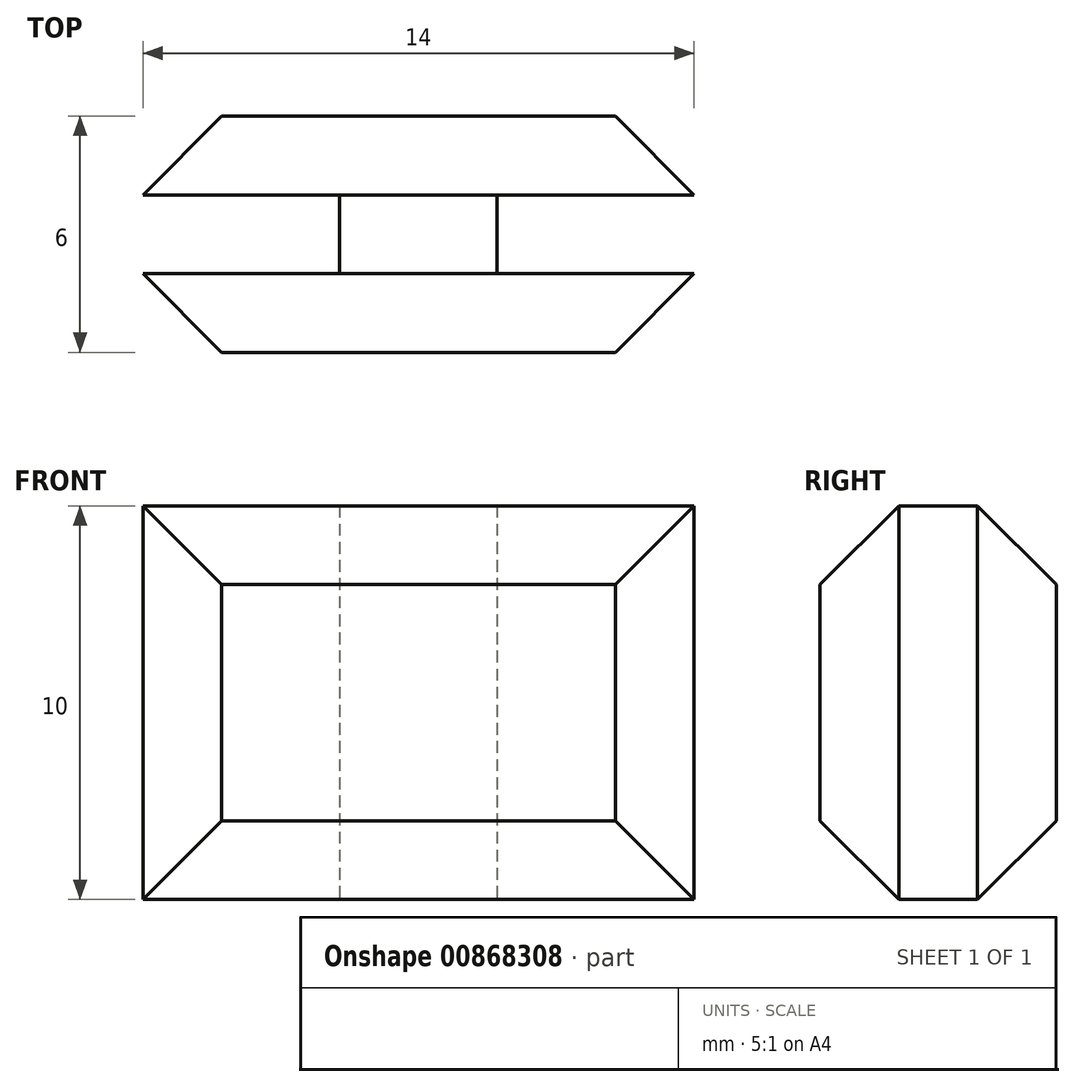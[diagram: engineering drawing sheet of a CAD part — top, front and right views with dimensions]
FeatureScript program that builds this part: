
annotation { "Feature Type Name" : "Feature", "Feature Type Description" : "" }
export const myFeature = defineFeature(function(context is Context, id is Id, definition is map)
    precondition{}
    {
        {
            var Q0;
            Q0=qCreatedBy(makeId("Top.planeOp"),FACE);
            var sketch = newSketch(context, id + "F0", { "sketchPlane" : qUnion([Q0])});
            skLineSegment(sketch, "E0.bottom", {"start": v(-7, 1) * mm, "end": v(7, 1) * mm});
            skLineSegment(sketch, "E0.top", {"start": v(-7, -1) * mm, "end": v(7, -1) * mm});
            skLineSegment(sketch, "E0.left", {"start": v(-7, 1) * mm, "end": v(-7, -1) * mm});
            skLineSegment(sketch, "E0.right", {"start": v(7, 1) * mm, "end": v(7, -1) * mm});
            skPoint(sketch, "E0.middle", {"position": v(0, 0) * mm});
            skLineSegment(sketch, "E1.top", {"start": v(-7, 3) * mm, "end": v(7, 3) * mm});
            skLineSegment(sketch, "E1.left", {"start": v(-7, 1) * mm, "end": v(-7, 3) * mm});
            skLineSegment(sketch, "E1.right", {"start": v(7, 1) * mm, "end": v(7, 3) * mm});
            skLineSegment(sketch, "E2.top", {"start": v(-7, -3) * mm, "end": v(7, -3) * mm});
            skLineSegment(sketch, "E2.left", {"start": v(-7, -1) * mm, "end": v(-7, -3) * mm});
            skLineSegment(sketch, "E2.right", {"start": v(7, -1) * mm, "end": v(7, -3) * mm});
            skLineSegment(sketch, "E3.bottom", {"start": v(-2, 1) * mm, "end": v(2, 1) * mm});
            skLineSegment(sketch, "E3.top", {"start": v(-2, -1) * mm, "end": v(2, -1) * mm});
            skLineSegment(sketch, "E3.left", {"start": v(-2, 1) * mm, "end": v(-2, -1) * mm});
            skLineSegment(sketch, "E3.right", {"start": v(2, 1) * mm, "end": v(2, -1) * mm});
            skSolve(sketch);
        }
        {
            var Q0;
            Q0=makeQuery(id+"F0.imprint","IMPRINT",FACE,{"disambiguationData":[TD([[makeQuery(id+"F0.imprint","IMPRINT",EDGE,{"derivedFrom":sQuery(id+"F0.wireOp",EDGE,"E1.top")}),-1.0]])]});
            var Q1;
            {var subQ2=sQuery(id+"F0.wireOp",EDGE,"E3.left");Q1=makeQuery(id+"F0.imprint","IMPRINT",FACE,{"disambiguationData":[TD([[makeQuery(id+"F0.imprint","IMPRINT",EDGE,{"derivedFrom":subQ2}),1.0]])]});}
            var Q2;
            Q2=makeQuery(id+"F0.imprint","IMPRINT",FACE,{"disambiguationData":[TD([[makeQuery(id+"F0.imprint","IMPRINT",EDGE,{"derivedFrom":sQuery(id+"F0.wireOp",EDGE,"E2.top")}),1.0]])]});
            extrude(context, id + "F1", {"entities" : qUnion([Q0, Q1, Q2]), "depth" : 10 * mm, "offsetDistance" : 25 * mm});
        }
        {
            var Q0;
            Q0=makeQuery(id+"F1.opExtrude","SWEPT_EDGE",EDGE,{"disambiguationData":[OSD([sQuery(id+"F0.wireOp",EDGE,"E1.top"),sQuery(id+"F0.wireOp",EDGE,"E1.left")])]});
            var Q1;
            Q1=makeQuery(id+"F1.opExtrude","SWEPT_EDGE",EDGE,{"disambiguationData":[OSD([sQuery(id+"F0.wireOp",EDGE,"E1.top"),sQuery(id+"F0.wireOp",EDGE,"E1.right")])]});
            var Q2;
            Q2=makeQuery(id+"F1.opExtrude","SWEPT_EDGE",EDGE,{"disambiguationData":[OSD([sQuery(id+"F0.wireOp",EDGE,"E2.top"),sQuery(id+"F0.wireOp",EDGE,"E2.right")])]});
            var Q3;
            Q3=makeQuery(id+"F1.opExtrude","SWEPT_EDGE",EDGE,{"disambiguationData":[OSD([sQuery(id+"F0.wireOp",EDGE,"E2.top"),sQuery(id+"F0.wireOp",EDGE,"E2.left")])]});
            chamfer(context, id + "F2", {"entities" : qUnion([Q0, Q1, Q2, Q3]), "width" : 2 * mm, "tangentPropagation" : true});
        }
        {
            var Q0;
            Q0=makeQuery(id+"F1.opExtrude","CAP_EDGE",EDGE,{"disambiguationData":[OSD([sQuery(id+"F0.wireOp",EDGE,"E1.top")])],"isStart":false});
            var Q1;
            Q1=makeQuery(id+"F1.opExtrude","CAP_EDGE",EDGE,{"disambiguationData":[OSD([sQuery(id+"F0.wireOp",EDGE,"E2.top")])],"isStart":false});
            var Q2;
            Q2=makeQuery(id+"F1.opExtrude","CAP_EDGE",EDGE,{"disambiguationData":[OSD([sQuery(id+"F0.wireOp",EDGE,"E2.top")])],"isStart":true});
            var Q3;
            Q3=makeQuery(id+"F1.opExtrude","CAP_EDGE",EDGE,{"disambiguationData":[OSD([sQuery(id+"F0.wireOp",EDGE,"E1.top")])],"isStart":true});
            chamfer(context, id + "F3", {"entities" : qUnion([Q0, Q1, Q2, Q3]), "width" : 2 * mm, "tangentPropagation" : true});
        }
    });
